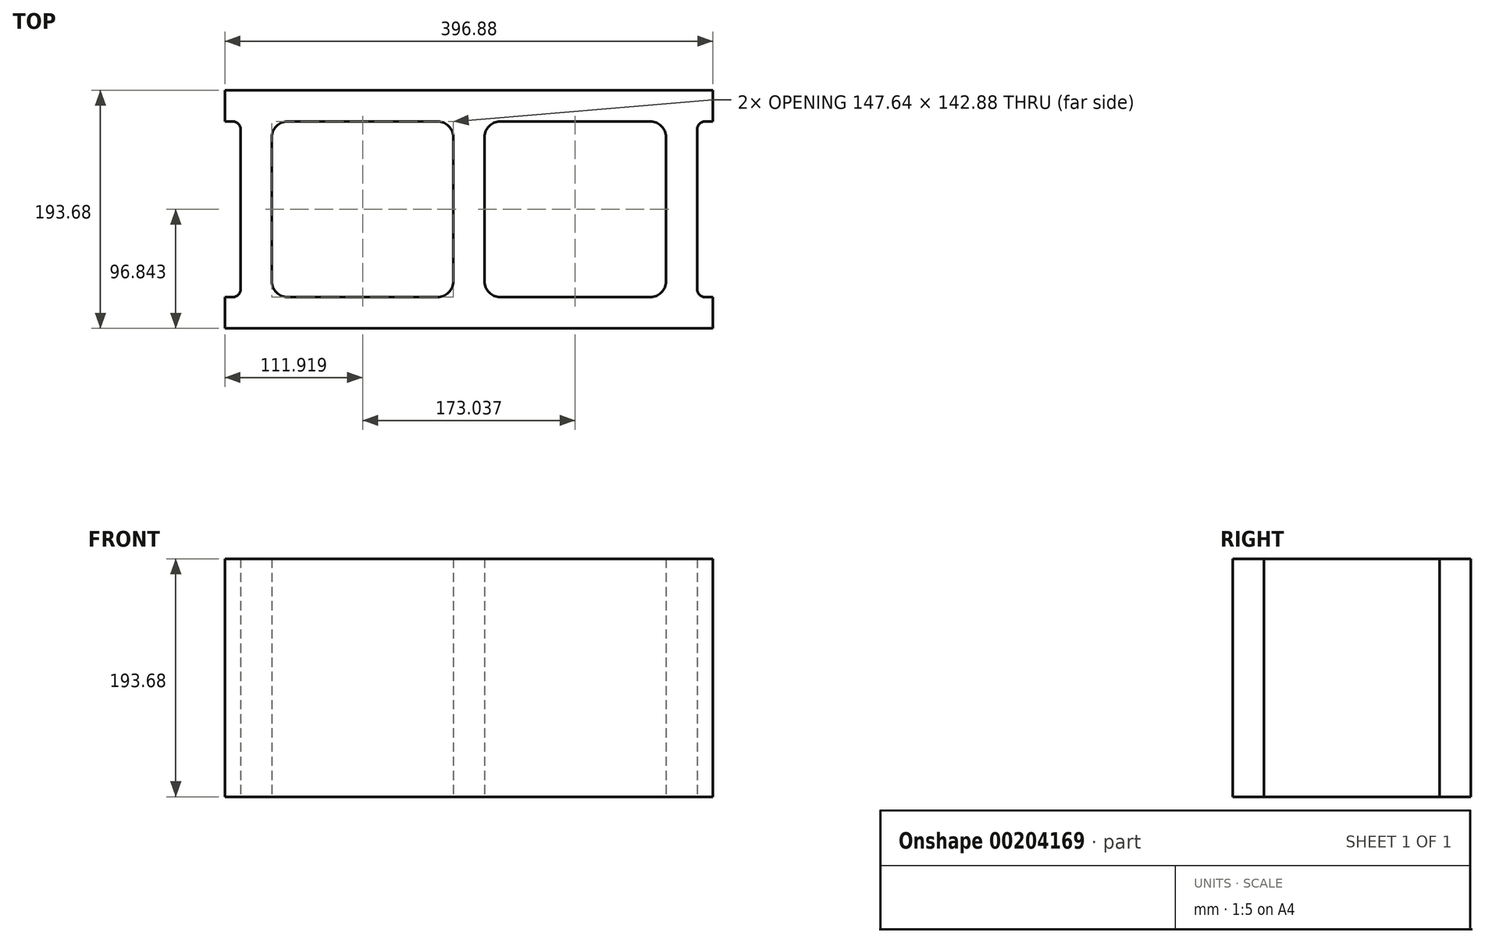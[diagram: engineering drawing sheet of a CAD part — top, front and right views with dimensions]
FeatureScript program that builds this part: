
annotation { "Feature Type Name" : "Feature", "Feature Type Description" : "" }
export const myFeature = defineFeature(function(context is Context, id is Id, definition is map)
    precondition{}
    {
        {
            var Q0;
            Q0=qCreatedBy(makeId("Top.planeOp"),FACE);
            var sketch = newSketch(context, id + "F0", { "sketchPlane" : qUnion([Q0])});
            skLineSegment(sketch, "E0", {"start": v(0, 0) * mm, "end": v(0, -25.4) * mm});
            skLineSegment(sketch, "E1", {"start": v(0, -193.67) * mm, "end": v(396.88, -193.67) * mm});
            skLineSegment(sketch, "E2", {"start": v(396.88, 0) * mm, "end": v(0, 0) * mm});
            skLineSegment(sketch, "E3.0", {"start": v(6.35, -25.4) * mm, "end": v(0, -25.4) * mm});
            skLineSegment(sketch, "E4.0", {"start": v(38.1, -96.84) * mm, "end": v(38.1, -155.58) * mm});
            skLineSegment(sketch, "E5.0", {"start": v(0, -168.28) * mm, "end": v(6.35, -168.28) * mm});
            skLineSegment(sketch, "E6.0", {"start": v(185.74, -38.1) * mm, "end": v(185.74, -155.58) * mm});
            skLineSegment(sketch, "E7.0", {"start": v(12.7, -31.75) * mm, "end": v(12.7, -161.93) * mm});
            skLineSegment(sketch, "E8", {"start": v(198.44, 0) * mm, "end": v(198.44, -193.67) * mm, "construction": true});
            skLineSegment(sketch, "E9", {"start": v(0, -96.84) * mm, "end": v(198.44, -96.84) * mm, "construction": true});
            skArc(sketch, "E10.filletArc", {"start": v(12.7, -31.75) * mm, "mid": v(10.84, -27.26) * mm, "end": v(6.35, -25.4) * mm});
            skArc(sketch, "E11.filletArc", {"start": v(6.35, -168.28) * mm, "mid": v(10.84, -166.42) * mm, "end": v(12.7, -161.93) * mm});
            skLineSegment(sketch, "E12", {"start": v(50.8, -25.4) * mm, "end": v(173.04, -25.4) * mm});
            skLineSegment(sketch, "E13", {"start": v(50.8, -168.28) * mm, "end": v(173.04, -168.28) * mm});
            skLineSegment(sketch, "E14", {"start": v(38.1, -96.84) * mm, "end": v(38.1, -38.1) * mm});
            skArc(sketch, "E15.filletArc", {"start": v(50.8, -25.4) * mm, "mid": v(41.82, -29.12) * mm, "end": v(38.1, -38.1) * mm});
            skArc(sketch, "E16.filletArc", {"start": v(38.1, -155.58) * mm, "mid": v(41.82, -164.56) * mm, "end": v(50.8, -168.28) * mm});
            skLineSegment(sketch, "E17.trimOffspring", {"start": v(0, -168.28) * mm, "end": v(0, -193.67) * mm});
            skArc(sketch, "E18.filletArc", {"start": v(185.74, -38.1) * mm, "mid": v(182.02, -29.12) * mm, "end": v(173.04, -25.4) * mm});
            skArc(sketch, "E19.filletArc", {"start": v(173.04, -168.28) * mm, "mid": v(182.02, -164.56) * mm, "end": v(185.74, -155.58) * mm});
            skArc(sketch, "E20.MirrorCS", {"start": v(390.53, -168.27) * mm, "mid": v(386.03, -166.42) * mm, "end": v(384.18, -161.92) * mm});
            skLineSegment(sketch, "E21.MirrorCS", {"start": v(396.88, -168.27) * mm, "end": v(390.53, -168.27) * mm});
            skArc(sketch, "E22.MirrorCS", {"start": v(384.18, -31.75) * mm, "mid": v(386.03, -27.26) * mm, "end": v(390.53, -25.4) * mm});
            skLineSegment(sketch, "E23.MirrorCS", {"start": v(390.53, -25.4) * mm, "end": v(396.88, -25.4) * mm});
            skArc(sketch, "E24.MirrorCS", {"start": v(358.78, -155.57) * mm, "mid": v(355.06, -164.56) * mm, "end": v(346.08, -168.27) * mm});
            skLineSegment(sketch, "E25.MirrorCS", {"start": v(346.08, -25.4) * mm, "end": v(223.84, -25.4) * mm});
            skLineSegment(sketch, "E26.MirrorCS", {"start": v(358.78, -96.84) * mm, "end": v(358.78, -38.1) * mm});
            skLineSegment(sketch, "E27.MirrorCS", {"start": v(396.88, 0) * mm, "end": v(396.88, -25.4) * mm});
            skArc(sketch, "E28.MirrorCS", {"start": v(346.08, -25.4) * mm, "mid": v(355.06, -29.12) * mm, "end": v(358.78, -38.1) * mm});
            skLineSegment(sketch, "E29.MirrorCS", {"start": v(384.18, -31.75) * mm, "end": v(384.18, -161.92) * mm});
            skArc(sketch, "E30.MirrorCS", {"start": v(223.84, -168.28) * mm, "mid": v(214.86, -164.56) * mm, "end": v(211.14, -155.58) * mm});
            skLineSegment(sketch, "E31.MirrorCS", {"start": v(358.78, -96.84) * mm, "end": v(358.78, -155.57) * mm});
            skArc(sketch, "E32.MirrorCS", {"start": v(211.14, -38.1) * mm, "mid": v(214.86, -29.12) * mm, "end": v(223.84, -25.4) * mm});
            skLineSegment(sketch, "E33.MirrorCS", {"start": v(346.08, -168.27) * mm, "end": v(223.84, -168.27) * mm});
            skLineSegment(sketch, "E34.MirrorCS", {"start": v(211.14, -38.1) * mm, "end": v(211.14, -155.58) * mm});
            skLineSegment(sketch, "E35.MirrorCS", {"start": v(396.88, -168.27) * mm, "end": v(396.88, -193.67) * mm});
            skSolve(sketch);
        }
        {
            var Q0;
            Q0=makeQuery(id+"F0.imprint","IMPRINT",FACE,{"disambiguationData":[TD([[makeQuery(id+"F0.imprint","IMPRINT",EDGE,{"derivedFrom":sQuery(id+"F0.wireOp",EDGE,"E0")}),1.0]])]});
            extrude(context, id + "F1", {"entities" : qUnion([Q0]), "depth" : 193.67 * mm});
        }
    });
